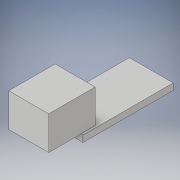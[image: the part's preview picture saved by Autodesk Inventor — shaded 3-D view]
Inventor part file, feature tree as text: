
AUTODESK INVENTOR PART (.ipt)
format: ipt  version: 2018 (Build 220112000, 112)  size: 107,008 bytes
history: native  units: in
note: dims shown in document units (in); Inventor stores cm internally (conversion verified against a paired STEP export)
features: extrude x2, sketch x2
ambient origin geometry x8: Origin, YZ Plane, XZ Plane, XY Plane, X Axis, Y Axis, Z Axis, Center Point
bodies: Solid1 (feature_tree)
feature tree (4):
  extrude  "Extrusion1"  Depth=1.378in
  extrude  "Extrusion2"  Depth=0.2165in
  sketch  "Sketch1"  dims[d0=0.6693in d1=1.378in]
  sketch  "Sketch2"  dims[d2=0.0984in d3=0.0in d4=0.2165in d5=0.0in d6=0.6102in d7=0.7087in d8=0.5118in d9=0.0in]
